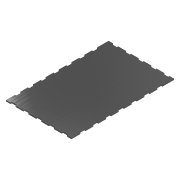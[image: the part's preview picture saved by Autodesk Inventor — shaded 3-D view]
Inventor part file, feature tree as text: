
AUTODESK INVENTOR PART (.ipt)
format: ipt  version: 2020 (Build 240168000, 168)  size: 233,472 bytes
history: native  units: in
note: dims shown in document units (in); Inventor stores cm internally (conversion verified against a paired STEP export)
features: extrude x3, sketch x3
ambient origin geometry x8: Origin, YZ Plane, XZ Plane, XY Plane, X Axis, Y Axis, Z Axis, Center Point
bodies: Solid1 (feature_tree)
feature tree (6):
  extrude  "base"  Depth=15.748in
  extrude  "Extrusion4"  Depth=0.7874in
  extrude  "Extrusion7"  Depth=1.9685in
  sketch  "Sketch1"  dims[d0=10.0394in d1=15.748in]
  sketch  "Sketch5"  dims[d2=0.1969in d3=0.0in d36=0.7874in]
  sketch  "Sketch8"  dims[d37=0.1969in d38=1.9685in d40=1.9685in d41=0.3937in d43=0.3937in d45=0.689in d46=0.689in d47=0.7874in d49=15.5512in d50=0.3937in d52=0.3937in d54=0.1969in d55=0.0in d82=0.1969in d83=0.7874in d84=1.378in d85=2.7559in d87=1.9685in d88=0.3937in d90=0.3937in d92=0.1969in d93=0.0in d34=0.0197in d35=0.0344in]
